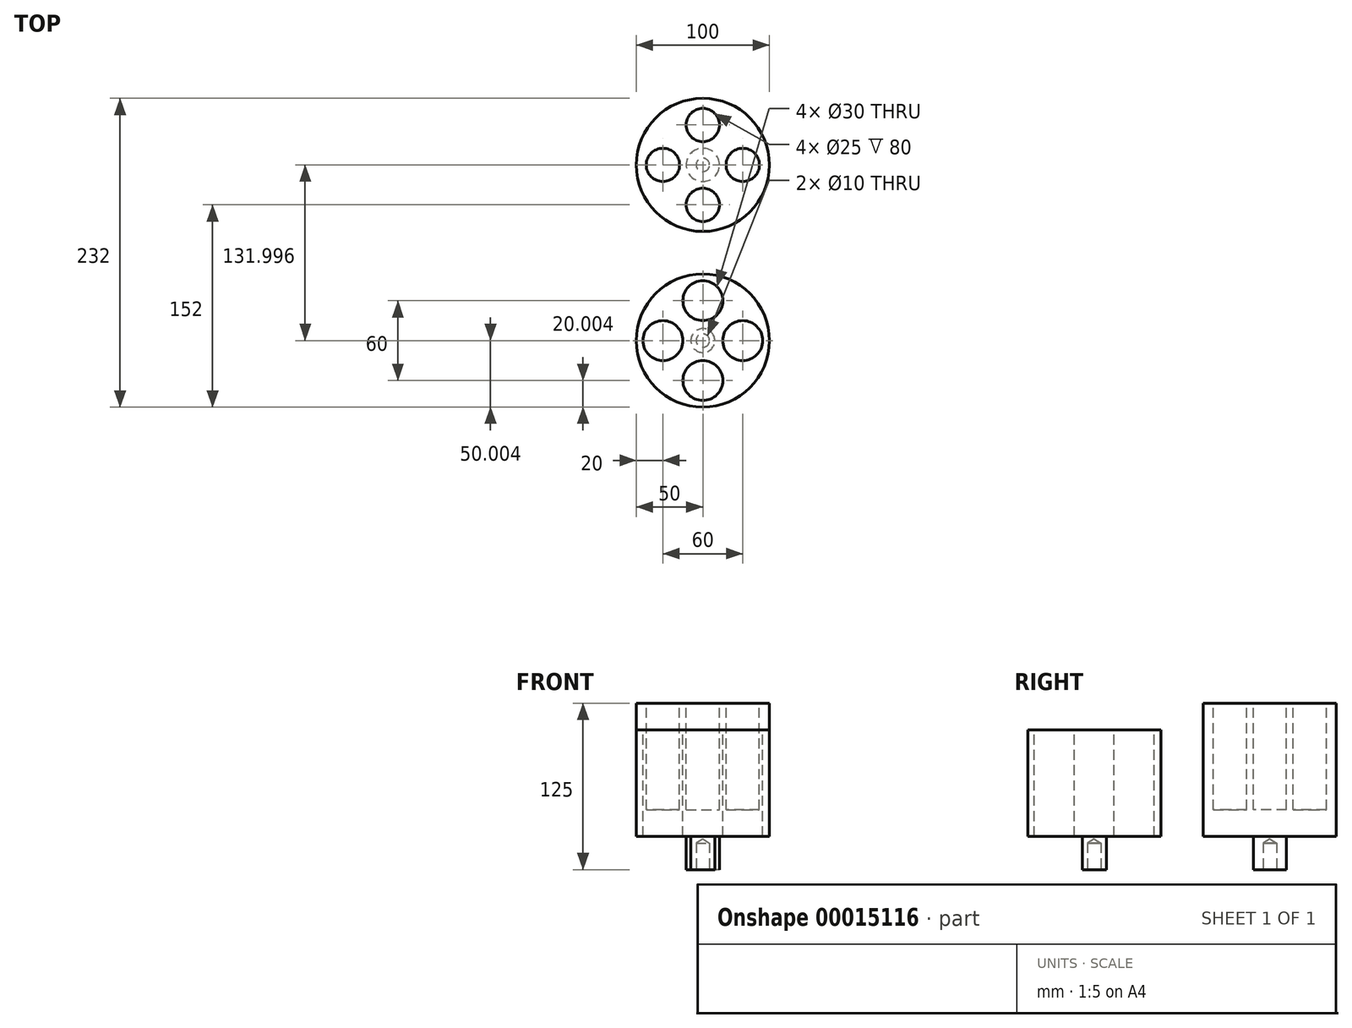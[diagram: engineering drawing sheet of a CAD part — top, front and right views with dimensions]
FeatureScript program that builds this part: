
annotation { "Feature Type Name" : "Feature", "Feature Type Description" : "" }
export const myFeature = defineFeature(function(context is Context, id is Id, definition is map)
    precondition{}
    {
        {
            var Q0;
            Q0=qCreatedBy(makeId("Top.planeOp"),FACE);
            var sketch = newSketch(context, id + "F0", { "sketchPlane" : qUnion([Q0])});
            skCircle(sketch, "E0", {"center": v(0, 0) * mm, "radius": 50 * mm});
            skCircle(sketch, "E1", {"center": v(0, 0) * mm, "radius": 12.5 * mm});
            skSolve(sketch);
        }
        {
            var Q0;
            Q0=makeQuery(id+"F0.imprint","IMPRINT",FACE,{"disambiguationData":[TD([[makeQuery(id+"F0.imprint","IMPRINT",EDGE,{"derivedFrom":sQuery(id+"F0.wireOp",EDGE,"E0")}),1.0]])]});
            var Q1;
            Q1=makeQuery(id+"F0.imprint","IMPRINT",FACE,{"disambiguationData":[TD([[makeQuery(id+"F0.imprint","IMPRINT",EDGE,{"derivedFrom":sQuery(id+"F0.wireOp",EDGE,"E1")}),1.0]])]});
            extrude(context, id + "F1", {"entities" : qUnion([Q0, Q1]), "depth" : 100 * mm});
        }
        {
            var Q0;
            Q0=makeQuery(id+"F0.imprint","IMPRINT",FACE,{"disambiguationData":[TD([[makeQuery(id+"F0.imprint","IMPRINT",EDGE,{"derivedFrom":sQuery(id+"F0.wireOp",EDGE,"E1")}),1.0]])]});
            extrude(context, id + "F2", {"entities" : qUnion([Q0]), "operationType" : NewBodyOperationType.ADD, "oppositeDirection" : true, "depth" : 25 * mm});
        }
        {
            var Q0;
            Q0=makeQuery(id+"F1.opExtrude","CAP_FACE",FACE,{"disambiguationData":[OSD([sQuery(id+"F0.wireOp",EDGE,"E0")])],"isStart":false});
            var sketch = newSketch(context, id + "F3", { "sketchPlane" : qUnion([Q0])});
            skCircle(sketch, "E2", {"center": v(0, 0) * mm, "radius": 30 * mm, "construction": true});
            skCircle(sketch, "E3", {"center": v(0, 30) * mm, "radius": 12.5 * mm});
            skSolve(sketch);
        }
        {
            var Q0;
            Q0=makeQuery(id+"F3.imprint","IMPRINT",FACE,{"disambiguationData":[TD([[makeQuery(id+"F3.imprint","IMPRINT",EDGE,{"derivedFrom":sQuery(id+"F3.wireOp",EDGE,"E3")}),1.0]])]});
            extrude(context, id + "F4", {"entities" : qUnion([Q0]), "operationType" : NewBodyOperationType.REMOVE, "oppositeDirection" : true, "depth" : 80 * mm});
        }
        {
            var Q0;
            Q0=makeQuery(id+"F4.boolean.opBoolean","COPY",FACE,{"derivedFrom":makeQuery(id+"F4.opExtrude","SWEPT_FACE",FACE,{"disambiguationData":[OSD([sQuery(id+"F3.wireOp",EDGE,"E3")])]})});
            var Q1;
            Q1=makeQuery(id+"F4.boolean.opBoolean","COPY",FACE,{"derivedFrom":makeQuery(id+"F4.opExtrude","CAP_FACE",FACE,{"disambiguationData":[OSD([sQuery(id+"F3.wireOp",EDGE,"E3")])],"isStart":false})});
            var Q2;
            Q2=makeQuery(id+"F1.opExtrude","SWEPT_FACE",FACE,{"disambiguationData":[OSD([sQuery(id+"F0.wireOp",EDGE,"E0")])]});
            circularPattern(context, id + "F5", {"faces" : qUnion([Q0, Q1]), "axis" : qUnion([Q2]), "angle" : 360 * degree, "instanceCount" : round(4), "equalSpace" : true, "patternType" : PatternType.FACE});
        }
        {
            var Q0;
            Q0=makeQuery(id+"F2.opExtrude","CAP_FACE",FACE,{"disambiguationData":[OSD([sQuery(id+"F0.wireOp",EDGE,"E1")])],"isStart":false});
            var sketch = newSketch(context, id + "F6", { "sketchPlane" : qUnion([Q0])});
            skCircle(sketch, "E4.0", {"center": v(0, 0) * mm, "radius": 12.5 * mm});
            skSolve(sketch);
        }
        {
            var Q0;
            Q0=sQuery(id+"F6.wireOp",VERTEX,"E4.0.center");
            var Q1;
            Q1=makeQuery(id+"F1.opExtrude","SWEPT_BODY",BODY,{"disambiguationData":[OSD([sQuery(id+"F0.wireOp",EDGE,"E0")])]});
            hole(context, id + "F7", {"style" : HoleStyle.SIMPLE, "holeDiameter" : 10 * mm, "endStyle" : HoleEndStyle.BLIND, "holeDepth" : 20 * mm, "locations" : qUnion([Q0]), "scope" : qUnion([Q1])});
        }
        {
            var Q0;
            Q0=qCreatedBy(makeId("Top.planeOp"),FACE);
            var sketch = newSketch(context, id + "F8", { "sketchPlane" : qUnion([Q0])});
            skCircle(sketch, "E5", {"center": v(0, -132) * mm, "radius": 50 * mm});
            skCircle(sketch, "E6", {"center": v(0, -132) * mm, "radius": 9 * mm});
            skSolve(sketch);
        }
        {
            var Q0;
            Q0=makeQuery(id+"F8.imprint","IMPRINT",FACE,{"disambiguationData":[TD([[makeQuery(id+"F8.imprint","IMPRINT",EDGE,{"derivedFrom":sQuery(id+"F8.wireOp",EDGE,"E6")}),1.0]])]});
            var Q1;
            Q1=makeQuery(id+"F8.imprint","IMPRINT",FACE,{"disambiguationData":[TD([[makeQuery(id+"F8.imprint","IMPRINT",EDGE,{"derivedFrom":sQuery(id+"F8.wireOp",EDGE,"E5")}),1.0]])]});
            extrude(context, id + "F9", {"entities" : qUnion([Q0, Q1]), "depth" : 80 * mm});
        }
        {
            var Q0;
            Q0=makeQuery(id+"F8.imprint","IMPRINT",FACE,{"disambiguationData":[TD([[makeQuery(id+"F8.imprint","IMPRINT",EDGE,{"derivedFrom":sQuery(id+"F8.wireOp",EDGE,"E6")}),1.0]])]});
            extrude(context, id + "F10", {"entities" : qUnion([Q0]), "operationType" : NewBodyOperationType.ADD, "oppositeDirection" : true, "depth" : 25 * mm});
        }
        {
            var Q0;
            Q0=makeQuery(id+"F9.opExtrude","CAP_FACE",FACE,{"disambiguationData":[OSD([sQuery(id+"F8.wireOp",EDGE,"E5")])],"isStart":false});
            var sketch = newSketch(context, id + "F11", { "sketchPlane" : qUnion([Q0])});
            skCircle(sketch, "E7", {"center": v(0, -132) * mm, "radius": 30 * mm, "construction": true});
            skCircle(sketch, "E8", {"center": v(30, -132) * mm, "radius": 15 * mm});
            skSolve(sketch);
        }
        {
            var Q0;
            Q0=makeQuery(id+"F11.imprint","IMPRINT",FACE,{"disambiguationData":[TD([[makeQuery(id+"F11.imprint","IMPRINT",EDGE,{"derivedFrom":sQuery(id+"F11.wireOp",EDGE,"E8")}),1.0]])]});
            extrude(context, id + "F12", {"entities" : qUnion([Q0]), "operationType" : NewBodyOperationType.REMOVE, "endBound" : BoundingType.THROUGH_ALL, "oppositeDirection" : true, "depth" : 25 * mm});
        }
        {
            var Q0;
            Q0=makeQuery(id+"F12.boolean.opBoolean","COPY",FACE,{"derivedFrom":makeQuery(id+"F12.opExtrude","SWEPT_FACE",FACE,{"disambiguationData":[OSD([sQuery(id+"F11.wireOp",EDGE,"E8")])]})});
            var Q1;
            Q1=makeQuery(id+"F9.opExtrude","SWEPT_FACE",FACE,{"disambiguationData":[OSD([sQuery(id+"F8.wireOp",EDGE,"E5")])]});
            circularPattern(context, id + "F13", {"faces" : qUnion([Q0]), "axis" : qUnion([Q1]), "angle" : 360 * degree, "instanceCount" : round(4), "equalSpace" : true, "patternType" : PatternType.FACE});
        }
        {
            var Q0;
            Q0=makeQuery(id+"F10.opExtrude","CAP_FACE",FACE,{"disambiguationData":[OSD([sQuery(id+"F8.wireOp",EDGE,"E6")])],"isStart":false});
            var sketch = newSketch(context, id + "F14", { "sketchPlane" : qUnion([Q0])});
            skCircle(sketch, "E9.0", {"center": v(0, 132) * mm, "radius": 9 * mm});
            skSolve(sketch);
        }
        {
            var Q0;
            Q0=sQuery(id+"F14.wireOp",VERTEX,"E9.0.center");
            var Q1;
            Q1=makeQuery(id+"F9.opExtrude","SWEPT_BODY",BODY,{"disambiguationData":[OSD([sQuery(id+"F8.wireOp",EDGE,"E5")])]});
            hole(context, id + "F15", {"style" : HoleStyle.SIMPLE, "holeDiameter" : 10 * mm, "endStyle" : HoleEndStyle.BLIND, "holeDepth" : 20 * mm, "locations" : qUnion([Q0]), "scope" : qUnion([Q1])});
        }
    });
